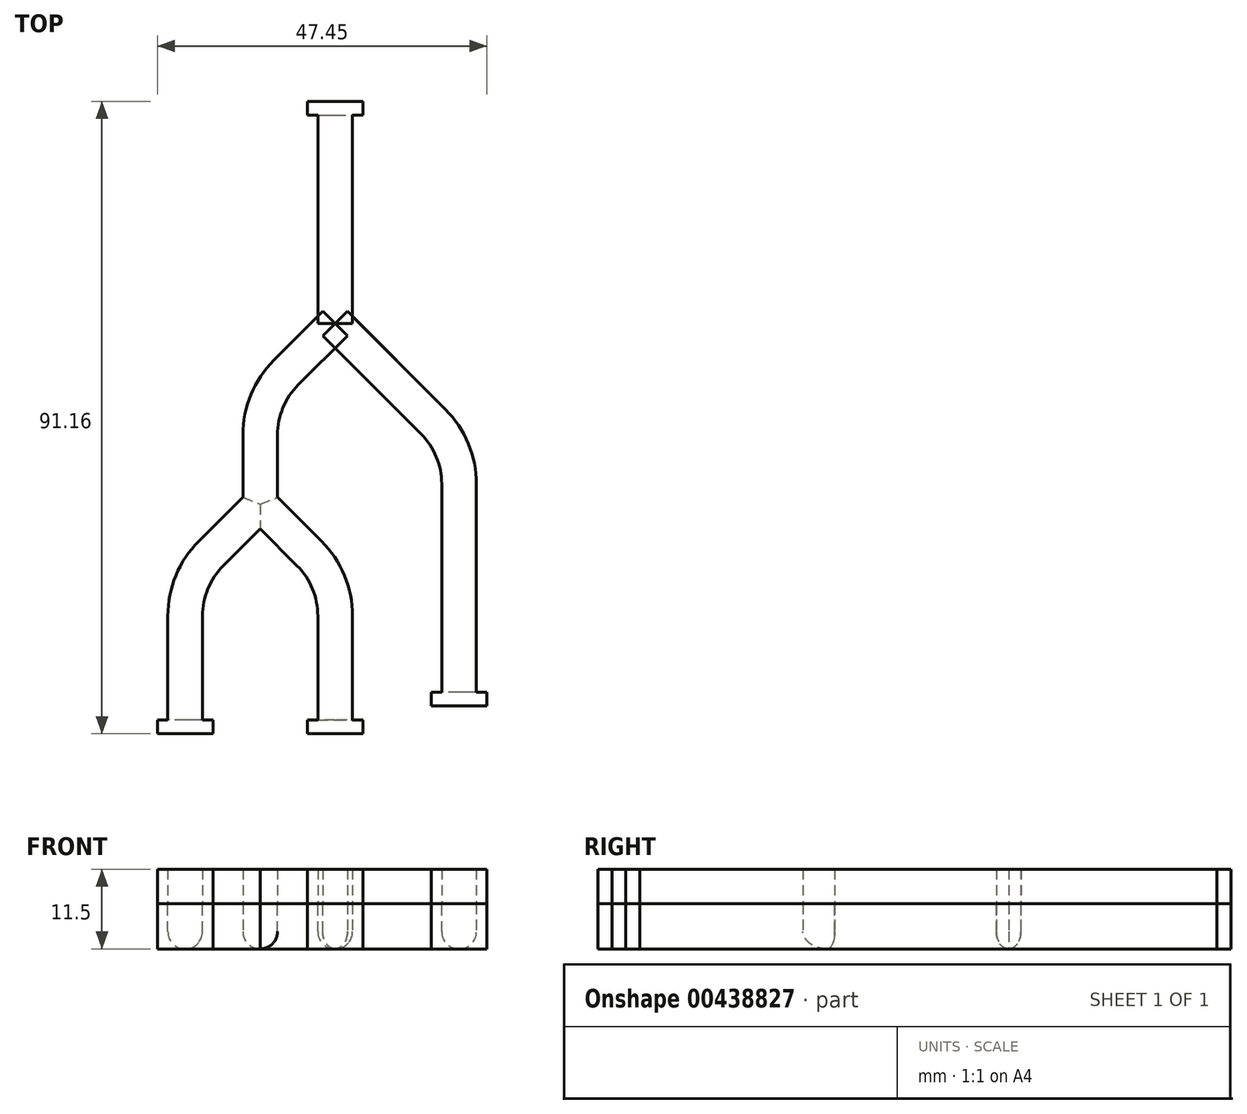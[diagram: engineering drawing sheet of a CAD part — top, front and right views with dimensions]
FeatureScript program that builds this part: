
annotation { "Feature Type Name" : "Feature", "Feature Type Description" : "" }
export const myFeature = defineFeature(function(context is Context, id is Id, definition is map)
    precondition{}
    {
        {
            var Q0;
            Q0=qCreatedBy(makeId("Front.planeOp"),FACE);
            var sketch = newSketch(context, id + "F0", { "sketchPlane" : qUnion([Q0])});
            skArc(sketch, "E0", {"start": v(0, -6.5) * mm, "mid": v(1.77, -5.77) * mm, "end": v(2.5, -4) * mm});
            skArc(sketch, "E1", {"start": v(0, -6.5) * mm, "mid": v(-1.77, -5.77) * mm, "end": v(-2.5, -4) * mm});
            skLineSegment(sketch, "E2", {"start": v(-2.5, -4) * mm, "end": v(-2.5, 0) * mm});
            skLineSegment(sketch, "E3", {"start": v(-2.5, 0) * mm, "end": v(2.5, 0) * mm});
            skLineSegment(sketch, "E4", {"start": v(2.5, 0) * mm, "end": v(2.5, -4) * mm});
            skSolve(sketch);
        }
        {
            var Q0;
            Q0 = qSketchRegion(id + "F0", true);
            extrude(context, id + "F1", {"entities" : qUnion([Q0]), "depth" : 30 * mm});
        }
        {
            var Q0;
            Q0=makeQuery(id+"F1.opExtrude","CAP_FACE",FACE,{"disambiguationData":[OSD([sQuery(id+"F0.wireOp",EDGE,"E0"),sQuery(id+"F0.wireOp",EDGE,"E1"),sQuery(id+"F0.wireOp",EDGE,"E2"),sQuery(id+"F0.wireOp",EDGE,"E3"),sQuery(id+"F0.wireOp",EDGE,"E4")])],"isStart":false});
            var sketch = newSketch(context, id + "F2", { "sketchPlane" : qUnion([Q0])});
            skLineSegment(sketch, "E5", {"start": v(0, 0) * mm, "end": v(0, -19.06) * mm});
            skPoint(sketch, "E5.endSnap0", {"position": v(0, -6.5) * mm});
            skSolve(sketch);
        }
        {
            var Q0;
            Q0 = qBodyType(qCreatedBy(id + "F2" ,EDGE), BodyType.WIRE);
            cPlane(context, id + "F3", {"entities" : qUnion([Q0]), "cplaneType" : CPlaneType.LINE_ANGLE, "offset" : 25 * mm, "angle" : 45 * degree, "width" : 150 * mm, "height" : 150 * mm});
        }
        {
            var Q0;
            {var subQ5=makeQuery(id+"F1.opExtrude","CAP_EDGE",EDGE,{"disambiguationData":[OSD([sQuery(id+"F0.wireOp",EDGE,"E2")])],"isStart":false});Q0=makeQuery(id+"F2.imprint","IMPRINT",FACE,{"disambiguationData":[TD([[makeQuery(id+"F2.imprint","IMPRINT",EDGE,{"derivedFrom":subQ5}),-1.0]])]});}
            var Q1;
            Q1 = qBodyType(qCreatedBy(id + "F2" ,EDGE), BodyType.WIRE);
            cPlane(context, id + "F4", {"entities" : qUnion([Q0, Q1]), "cplaneType" : CPlaneType.LINE_ANGLE, "offset" : 25 * mm, "angle" : 45 * degree, "width" : 150 * mm, "height" : 150 * mm});
        }
        {
            var Q0;
            Q0=qCreatedBy(id+"F3.planeOp",FACE);
            var sketch = newSketch(context, id + "F5", { "sketchPlane" : qUnion([Q0])});
            skArc(sketch, "E6", {"start": v(21.24, -6.5) * mm, "mid": v(19.47, -5.77) * mm, "end": v(18.74, -4) * mm});
            skArc(sketch, "E7", {"start": v(21.24, -6.5) * mm, "mid": v(23, -5.77) * mm, "end": v(23.74, -4) * mm});
            skLineSegment(sketch, "E8", {"start": v(23.74, -4) * mm, "end": v(23.74, 0) * mm});
            skLineSegment(sketch, "E9", {"start": v(23.74, 0) * mm, "end": v(18.74, 0) * mm});
            skLineSegment(sketch, "E10", {"start": v(18.74, 0) * mm, "end": v(18.74, -4) * mm});
            skPoint(sketch, "E11.start.orphan", {"position": v(21.24, 0) * mm});
            skSolve(sketch);
        }
        {
            var Q0;
            Q0=qCreatedBy(makeId("Top.planeOp"),FACE);
            var sketch = newSketch(context, id + "F6", { "sketchPlane" : qUnion([Q0])});
            skLineSegment(sketch, "E12", {"start": v(0, -30) * mm, "end": v(14.14, -44.14) * mm});
            skArc(sketch, "E13", {"start": v(14.14, -44.14) * mm, "mid": v(16.9, -48.27) * mm, "end": v(17.87, -53.15) * mm});
            skLineSegment(sketch, "E14", {"start": v(17.87, -53.15) * mm, "end": v(17.87, -83.15) * mm});
            skSolve(sketch);
        }
        {
            var Q0;
            Q0 = qSketchRegion(id + "F5", true);
            var Q1;
            Q1 = qConstructionFilter(qBodyType(qCreatedBy(id + "F6" ,EDGE), BodyType.WIRE), ConstructionObject.NO);
            sweep(context, id + "F7", {"profiles" : qUnion([Q0]), "path" : qUnion([Q1])});
        }
        {
            var Q0;
            Q0=qCreatedBy(id+"F4.planeOp",FACE);
            var sketch = newSketch(context, id + "F8", { "sketchPlane" : qUnion([Q0])});
            skArc(sketch, "E15", {"start": v(-21.21, -6.5) * mm, "mid": v(-22.98, -5.77) * mm, "end": v(-23.71, -4) * mm});
            skArc(sketch, "E16", {"start": v(-21.21, -6.5) * mm, "mid": v(-19.45, -5.77) * mm, "end": v(-18.71, -4) * mm});
            skLineSegment(sketch, "E17", {"start": v(-18.71, -4) * mm, "end": v(-18.71, 0) * mm});
            skLineSegment(sketch, "E18", {"start": v(-18.71, 0) * mm, "end": v(-23.71, 0) * mm});
            skLineSegment(sketch, "E19", {"start": v(-23.71, 0) * mm, "end": v(-23.71, -4) * mm});
            skPoint(sketch, "E20.start.orphan", {"position": v(-21.21, 0) * mm});
            skSolve(sketch);
        }
        {
            var Q0;
            Q0=qCreatedBy(makeId("Top.planeOp"),FACE);
            var sketch = newSketch(context, id + "F9", { "sketchPlane" : qUnion([Q0])});
            skLineSegment(sketch, "E21", {"start": v(0, -30) * mm, "end": v(-7.07, -37.07) * mm});
            skArc(sketch, "E22", {"start": v(-7.07, -37.07) * mm, "mid": v(-9.83, -41.2) * mm, "end": v(-10.8, -46.08) * mm});
            skLineSegment(sketch, "E23", {"start": v(-10.8, -46.08) * mm, "end": v(-10.8, -56.08) * mm});
            skSolve(sketch);
        }
        {
            var Q0;
            Q0 = qSketchRegion(id + "F8", true);
            var Q1;
            Q1 = qConstructionFilter(qBodyType(qCreatedBy(id + "F9" ,EDGE), BodyType.WIRE), ConstructionObject.NO);
            sweep(context, id + "F10", {"profiles" : qUnion([Q0]), "path" : qUnion([Q1])});
        }
        {
            var Q0;
            Q0=makeQuery(id+"F10.opSweep","CAP_FACE",FACE,{"disambiguationData":[OSD([sQuery(id+"F8.wireOp",EDGE,"E15"),sQuery(id+"F8.wireOp",EDGE,"E16"),sQuery(id+"F8.wireOp",EDGE,"E17"),sQuery(id+"F8.wireOp",EDGE,"E18"),sQuery(id+"F8.wireOp",EDGE,"E19"),sQuery(id+"F9.wireOp",VERTEX,"E23.end")])],"isStart":false});
            var sketch = newSketch(context, id + "F11", { "sketchPlane" : qUnion([Q0])});
            skLineSegment(sketch, "E24", {"start": v(-10.8, 0) * mm, "end": v(-10.8, -6.84) * mm});
            skPoint(sketch, "E24.endSnap0", {"position": v(-10.8, -6.5) * mm});
            skSolve(sketch);
        }
        {
            var Q0;
            {var subQ1=sQuery(id+"F9.wireOp",VERTEX,"E23.end");var subQ6=makeQuery(id+"F10.opSweep","CAP_EDGE",EDGE,{"disambiguationData":[OSD([sQuery(id+"F8.wireOp",EDGE,"E17"),subQ1])],"isStart":false});Q0=makeQuery(id+"F11.imprint","IMPRINT",FACE,{"disambiguationData":[TD([[makeQuery(id+"F11.imprint","IMPRINT",EDGE,{"derivedFrom":subQ6}),1.0]])]});}
            var Q1;
            Q1 = qBodyType(qCreatedBy(id + "F11" ,EDGE), BodyType.WIRE);
            cPlane(context, id + "F12", {"entities" : qUnion([Q0, Q1]), "cplaneType" : CPlaneType.LINE_ANGLE, "offset" : 25 * mm, "angle" : 45 * degree, "width" : 150 * mm, "height" : 150 * mm});
        }
        {
            var Q0;
            Q0 = qBodyType(qCreatedBy(id + "F11" ,EDGE), BodyType.WIRE);
            var Q1;
            {var subQ1=sQuery(id+"F9.wireOp",VERTEX,"E23.end");var subQ6=makeQuery(id+"F10.opSweep","CAP_EDGE",EDGE,{"disambiguationData":[OSD([sQuery(id+"F8.wireOp",EDGE,"E17"),subQ1])],"isStart":false});Q1=makeQuery(id+"F11.imprint","IMPRINT",FACE,{"disambiguationData":[TD([[makeQuery(id+"F11.imprint","IMPRINT",EDGE,{"derivedFrom":subQ6}),1.0]])]});}
            cPlane(context, id + "F13", {"entities" : qUnion([Q0, Q1]), "cplaneType" : CPlaneType.LINE_ANGLE, "offset" : 25 * mm, "angle" : 135 * degree, "width" : 150 * mm, "height" : 150 * mm});
        }
        {
            var Q0;
            Q0=qCreatedBy(id+"F12.planeOp",FACE);
            var sketch = newSketch(context, id + "F14", { "sketchPlane" : qUnion([Q0])});
            skPoint(sketch, "E25.start.orphan", {"position": v(-31.98, 0) * mm});
            skPoint(sketch, "E26.end.orphan", {"position": v(-29.5, 2.32) * mm});
            skPoint(sketch, "E27.center.orphan", {"position": v(-32, 2.32) * mm});
            skPoint(sketch, "E28.end.orphan", {"position": v(-34.5, 2.32) * mm});
            skPoint(sketch, "E29.start.orphan", {"position": v(-29.52, 0) * mm});
            skLineSegment(sketch, "E30", {"start": v(-32.02, 0) * mm, "end": v(-32.02, -4) * mm});
            skLineSegment(sketch, "E31", {"start": v(-32.02, -4) * mm, "end": v(-32, -6.5) * mm});
            skArc(sketch, "E32", {"start": v(-32, -6.5) * mm, "mid": v(-33.78, -5.77) * mm, "end": v(-34.52, -4) * mm});
            skArc(sketch, "E33", {"start": v(-32, -6.5) * mm, "mid": v(-30.24, -5.76) * mm, "end": v(-29.52, -4) * mm});
            skLineSegment(sketch, "E34", {"start": v(-29.52, -4) * mm, "end": v(-29.52, 0) * mm});
            skLineSegment(sketch, "E35", {"start": v(-34.52, -4) * mm, "end": v(-34.52, 0) * mm});
            skLineSegment(sketch, "E36", {"start": v(-34.52, 0) * mm, "end": v(-29.52, 0) * mm});
            skSolve(sketch);
        }
        {
            var Q0;
            Q0=qCreatedBy(makeId("Top.planeOp"),FACE);
            var sketch = newSketch(context, id + "F15", { "sketchPlane" : qUnion([Q0])});
            skLineSegment(sketch, "E37", {"start": v(-10.8, -56.08) * mm, "end": v(-17.87, -63.15) * mm});
            skArc(sketch, "E38", {"start": v(-17.87, -63.15) * mm, "mid": v(-20.63, -67.28) * mm, "end": v(-21.6, -72.16) * mm});
            skLineSegment(sketch, "E39", {"start": v(-21.6, -72.16) * mm, "end": v(-21.6, -87.16) * mm});
            skSolve(sketch);
        }
        {
            var Q0;
            Q0 = qSketchRegion(id + "F14", true);
            var Q1;
            Q1 = qConstructionFilter(qBodyType(qCreatedBy(id + "F15" ,EDGE), BodyType.WIRE), ConstructionObject.NO);
            sweep(context, id + "F16", {"operationType" : NewBodyOperationType.ADD, "profiles" : qUnion([Q0]), "path" : qUnion([Q1])});
        }
        {
            var Q0;
            Q0=qCreatedBy(id+"F13.planeOp",FACE);
            var sketch = newSketch(context, id + "F17", { "sketchPlane" : qUnion([Q0])});
            skArc(sketch, "E40", {"start": v(-47.3, -6.5) * mm, "mid": v(-45.52, -5.77) * mm, "end": v(-44.8, -4) * mm});
            skArc(sketch, "E41", {"start": v(-47.3, -6.5) * mm, "mid": v(-49.06, -5.77) * mm, "end": v(-49.8, -4) * mm});
            skLineSegment(sketch, "E42", {"start": v(-49.8, -4) * mm, "end": v(-49.8, 0) * mm});
            skLineSegment(sketch, "E43", {"start": v(-49.8, 0) * mm, "end": v(-44.8, 0) * mm});
            skLineSegment(sketch, "E44", {"start": v(-44.8, 0) * mm, "end": v(-44.8, -4) * mm});
            skPoint(sketch, "E45.start.orphan", {"position": v(-47.3, 0) * mm});
            skSolve(sketch);
        }
        {
            var Q0;
            Q0=makeQuery(id+"F16.boolean.opBoolean","MERGE",FACE,{"derivedFrom":[makeQuery(id+"F10.opSweep","SWEPT_FACE",FACE,{"disambiguationData":[OSD([sQuery(id+"F8.wireOp",EDGE,"E18"),sQuery(id+"F9.wireOp",EDGE,"E21")])]}),makeQuery(id+"F16.opSweep","SWEPT_FACE",FACE,{"disambiguationData":[OSD([sQuery(id+"F14.wireOp",EDGE,"E36"),sQuery(id+"F15.wireOp",EDGE,"E37")])]})]});
            var sketch = newSketch(context, id + "F18", { "sketchPlane" : qUnion([Q0])});
            skLineSegment(sketch, "E46", {"start": v(-10.8, -56.08) * mm, "end": v(-3.73, -63.15) * mm});
            skArc(sketch, "E47", {"start": v(-3.73, -63.15) * mm, "mid": v(-0.97, -67.28) * mm, "end": v(0, -72.16) * mm});
            skLineSegment(sketch, "E48", {"start": v(0, -72.16) * mm, "end": v(0, -87.16) * mm});
            skSolve(sketch);
        }
        {
            var Q0;
            Q0 = qSketchRegion(id + "F17", true);
            var Q1;
            Q1 = qConstructionFilter(qBodyType(qCreatedBy(id + "F18" ,EDGE), BodyType.WIRE), ConstructionObject.NO);
            sweep(context, id + "F19", {"operationType" : NewBodyOperationType.ADD, "profiles" : qUnion([Q0]), "path" : qUnion([Q1])});
        }
        {
            var Q0;
            Q0=makeQuery(id+"F19.opSweep","CAP_FACE",FACE,{"disambiguationData":[OSD([sQuery(id+"F17.wireOp",EDGE,"E40"),sQuery(id+"F17.wireOp",EDGE,"E41"),sQuery(id+"F17.wireOp",EDGE,"E42"),sQuery(id+"F17.wireOp",EDGE,"E43"),sQuery(id+"F17.wireOp",EDGE,"E44"),sQuery(id+"F18.wireOp",VERTEX,"E48.end")])],"isStart":false});
            var sketch = newSketch(context, id + "F20", { "sketchPlane" : qUnion([Q0])});
            skLineSegment(sketch, "E49", {"start": v(0, 0) * mm, "end": v(4, 0) * mm});
            skLineSegment(sketch, "E50", {"start": v(4, 0) * mm, "end": v(4, -6.5) * mm});
            skLineSegment(sketch, "E51", {"start": v(4, -6.5) * mm, "end": v(0, -6.5) * mm});
            skLineSegment(sketch, "E52", {"start": v(0, -6.5) * mm, "end": v(-4, -6.5) * mm});
            skLineSegment(sketch, "E53", {"start": v(-4, -6.5) * mm, "end": v(-4, 0) * mm});
            skLineSegment(sketch, "E54", {"start": v(-4, 0) * mm, "end": v(0, 0) * mm});
            skSolve(sketch);
        }
        {
            var Q0;
            Q0 = qSketchRegion(id + "F20", true);
            extrude(context, id + "F21", {"entities" : qUnion([Q0]), "operationType" : NewBodyOperationType.ADD, "depth" : 2 * mm});
        }
        {
            var Q0;
            Q0=makeQuery(id+"F16.opSweep","CAP_FACE",FACE,{"disambiguationData":[OSD([sQuery(id+"F14.wireOp",EDGE,"E32"),sQuery(id+"F14.wireOp",EDGE,"E33"),sQuery(id+"F14.wireOp",EDGE,"E34"),sQuery(id+"F14.wireOp",EDGE,"E35"),sQuery(id+"F14.wireOp",EDGE,"E36"),sQuery(id+"F15.wireOp",VERTEX,"E39.end")])],"isStart":false});
            var sketch = newSketch(context, id + "F22", { "sketchPlane" : qUnion([Q0])});
            skLineSegment(sketch, "E55", {"start": v(-24.1, 0) * mm, "end": v(-21.6, 0) * mm});
            skLineSegment(sketch, "E56", {"start": v(-21.6, 0) * mm, "end": v(-17.6, 0) * mm});
            skLineSegment(sketch, "E57", {"start": v(-17.6, 0) * mm, "end": v(-17.6, -6.5) * mm});
            skLineSegment(sketch, "E58", {"start": v(-17.6, -6.5) * mm, "end": v(-25.6, -6.5) * mm});
            skLineSegment(sketch, "E59", {"start": v(-25.6, -6.5) * mm, "end": v(-25.6, 0) * mm});
            skLineSegment(sketch, "E60", {"start": v(-25.6, 0) * mm, "end": v(-21.6, 0) * mm});
            skSolve(sketch);
        }
        {
            var Q0;
            Q0 = qSketchRegion(id + "F22", true);
            extrude(context, id + "F23", {"entities" : qUnion([Q0]), "operationType" : NewBodyOperationType.ADD, "depth" : 2 * mm});
        }
        {
            var Q0;
            Q0=makeQuery(id+"F7.opSweep","CAP_FACE",FACE,{"disambiguationData":[OSD([sQuery(id+"F5.wireOp",EDGE,"E6"),sQuery(id+"F5.wireOp",EDGE,"E7"),sQuery(id+"F5.wireOp",EDGE,"E8"),sQuery(id+"F5.wireOp",EDGE,"E9"),sQuery(id+"F5.wireOp",EDGE,"E10"),sQuery(id+"F6.wireOp",VERTEX,"wUwuH1Yi-qAGJ-ZlKk-6PMT-0EflDv7uNIR9.end")])],"isStart":false});
            var sketch = newSketch(context, id + "F24", { "sketchPlane" : qUnion([Q0])});
            skLineSegment(sketch, "E61", {"start": v(17.85, 0) * mm, "end": v(21.85, 0) * mm});
            skLineSegment(sketch, "E62", {"start": v(21.85, 0) * mm, "end": v(21.85, -6.5) * mm});
            skLineSegment(sketch, "E63", {"start": v(21.85, -6.5) * mm, "end": v(13.85, -6.5) * mm});
            skLineSegment(sketch, "E64", {"start": v(13.85, -6.5) * mm, "end": v(13.85, 0) * mm});
            skLineSegment(sketch, "E65", {"start": v(13.85, 0) * mm, "end": v(17.85, 0) * mm});
            skSolve(sketch);
        }
        {
            var Q0;
            Q0 = qSketchRegion(id + "F24", true);
            extrude(context, id + "F25", {"entities" : qUnion([Q0]), "operationType" : NewBodyOperationType.ADD, "depth" : 2 * mm});
        }
        {
            var Q0;
            Q0=makeQuery(id+"F1.opExtrude","CAP_FACE",FACE,{"disambiguationData":[OSD([sQuery(id+"F0.wireOp",EDGE,"E0"),sQuery(id+"F0.wireOp",EDGE,"E1"),sQuery(id+"F0.wireOp",EDGE,"E2"),sQuery(id+"F0.wireOp",EDGE,"E3"),sQuery(id+"F0.wireOp",EDGE,"E4")])],"isStart":true});
            var sketch = newSketch(context, id + "F26", { "sketchPlane" : qUnion([Q0])});
            skLineSegment(sketch, "E66", {"start": v(0, 0) * mm, "end": v(4, 0) * mm});
            skLineSegment(sketch, "E67", {"start": v(4, 0) * mm, "end": v(4, -6.5) * mm});
            skLineSegment(sketch, "E68", {"start": v(4, -6.5) * mm, "end": v(-4, -6.5) * mm});
            skLineSegment(sketch, "E69", {"start": v(-4, -6.5) * mm, "end": v(-4, 0) * mm});
            skLineSegment(sketch, "E70", {"start": v(-4, 0) * mm, "end": v(0, 0) * mm});
            skSolve(sketch);
        }
        {
            var Q0;
            Q0 = qSketchRegion(id + "F26", true);
            extrude(context, id + "F27", {"entities" : qUnion([Q0]), "operationType" : NewBodyOperationType.ADD, "depth" : 2 * mm});
        }
        {
            var Q0;
            Q0=makeQuery(id+"F23.boolean.opBoolean","MERGE",FACE,{"derivedFrom":[makeQuery(id+"F21.boolean.opBoolean","MERGE",FACE,{"derivedFrom":[makeQuery(id+"F19.boolean.opBoolean","MERGE",FACE,{"derivedFrom":[makeQuery(id+"F16.boolean.opBoolean","MERGE",FACE,{"derivedFrom":[makeQuery(id+"F10.opSweep","SWEPT_FACE",FACE,{"disambiguationData":[OSD([sQuery(id+"F8.wireOp",EDGE,"E18"),sQuery(id+"F9.wireOp",EDGE,"E21")])]}),makeQuery(id+"F16.opSweep","SWEPT_FACE",FACE,{"disambiguationData":[OSD([sQuery(id+"F14.wireOp",EDGE,"E36"),sQuery(id+"F15.wireOp",EDGE,"E37")])]})]}),makeQuery(id+"F19.opSweep","SWEPT_FACE",FACE,{"disambiguationData":[OSD([sQuery(id+"F17.wireOp",EDGE,"E43"),sQuery(id+"F18.wireOp",EDGE,"E46")])]})]}),makeQuery(id+"F21.opExtrude","SWEPT_FACE",FACE,{"disambiguationData":[OSD([sQuery(id+"F20.wireOp",EDGE,"E49"),sQuery(id+"F20.wireOp",EDGE,"E54")])]})]}),makeQuery(id+"F23.opExtrude","SWEPT_FACE",FACE,{"disambiguationData":[OSD([sQuery(id+"F22.wireOp",EDGE,"E56"),sQuery(id+"F22.wireOp",EDGE,"E60")])]})]});
            var Q1;
            Q1=makeQuery(id+"F25.boolean.opBoolean","MERGE",FACE,{"derivedFrom":[makeQuery(id+"F7.opSweep","SWEPT_FACE",FACE,{"disambiguationData":[OSD([sQuery(id+"F5.wireOp",EDGE,"E9"),sQuery(id+"F6.wireOp",EDGE,"E12")])]}),makeQuery(id+"F25.opExtrude","SWEPT_FACE",FACE,{"disambiguationData":[OSD([sQuery(id+"F24.wireOp",EDGE,"E61"),sQuery(id+"F24.wireOp",EDGE,"E65")])]})]});
            var Q2;
            Q2=makeQuery(id+"F27.boolean.opBoolean","MERGE",FACE,{"derivedFrom":[makeQuery(id+"F1.opExtrude","SWEPT_FACE",FACE,{"disambiguationData":[OSD([sQuery(id+"F0.wireOp",EDGE,"E3")])]}),makeQuery(id+"F27.opExtrude","SWEPT_FACE",FACE,{"disambiguationData":[OSD([sQuery(id+"F26.wireOp",EDGE,"E66"),sQuery(id+"F26.wireOp",EDGE,"E70")])]})]});
            extrude(context, id + "F28", {"entities" : qUnion([Q0, Q1, Q2]), "depth" : 5 * mm});
        }
    });
